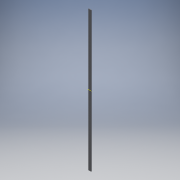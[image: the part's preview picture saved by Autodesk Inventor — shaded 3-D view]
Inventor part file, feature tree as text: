
AUTODESK INVENTOR PART (.ipt)
format: ipt  version: 2018 (Build 220112000, 112)  size: 96,256 bytes
history: native  units: mm
features: extrude x1, other x1, sketch x1
ambient origin geometry x8: Origin, YZ Plane, XZ Plane, XY Plane, X Axis, Y Axis, Z Axis, Center Point
bodies: Solid1 (feature_tree)
feature tree (3):
  extrude  "Extrusion1"  Depth=5.0mm
  other  "Work Axis1"
  sketch  "Sketch1"  dims[d0=25.0mm d1=5.0mm d2=1208.95mm d3=0.0mm]
